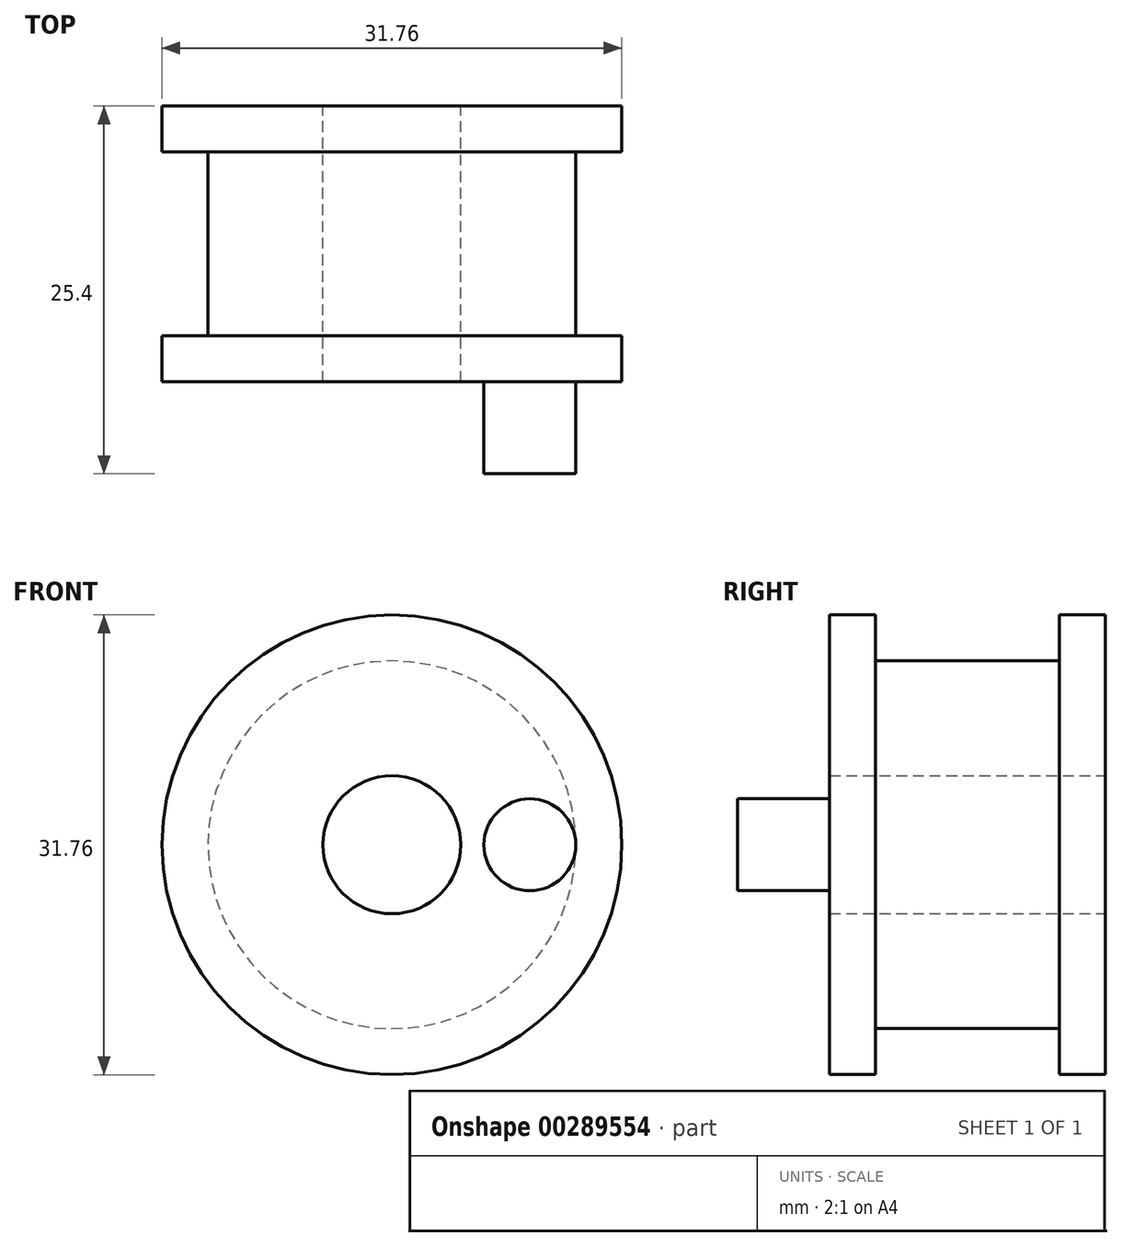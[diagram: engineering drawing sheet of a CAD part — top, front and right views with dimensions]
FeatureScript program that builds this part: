
annotation { "Feature Type Name" : "Feature", "Feature Type Description" : "" }
export const myFeature = defineFeature(function(context is Context, id is Id, definition is map)
    precondition{}
    {
        {
            var Q0;
            Q0=qCreatedBy(makeId("Front.planeOp"),FACE);
            var sketch = newSketch(context, id + "F0", { "sketchPlane" : qUnion([Q0])});
            skCircle(sketch, "E0", {"center": v(0, 0) * mm, "radius": 15.88 * mm});
            skCircle(sketch, "E1", {"center": v(0, 0) * mm, "radius": 4.76 * mm});
            skCircle(sketch, "E2", {"center": v(0, 0) * mm, "radius": 12.7 * mm});
            skSolve(sketch);
        }
        {
            var Q0;
            Q0=makeQuery(id+"F0.imprint","IMPRINT",FACE,{"disambiguationData":[TD([[makeQuery(id+"F0.imprint","IMPRINT",EDGE,{"derivedFrom":sQuery(id+"F0.wireOp",EDGE,"E0")}),1.0]])]});
            extrude(context, id + "F1", {"entities" : qUnion([Q0]), "depth" : 3.17 * mm});
        }
        {
            var Q0;
            Q0=makeQuery(id+"F0.imprint","IMPRINT",FACE,{"disambiguationData":[TD([[makeQuery(id+"F0.imprint","IMPRINT",EDGE,{"derivedFrom":sQuery(id+"F0.wireOp",EDGE,"E1")}),-1.0]])]});
            extrude(context, id + "F2", {"entities" : qUnion([Q0]), "operationType" : NewBodyOperationType.ADD, "depth" : 19.05 * mm});
        }
        {
            var Q0;
            Q0=makeQuery(id+"F2.opExtrude","CAP_FACE",FACE,{"disambiguationData":[OSD([sQuery(id+"F0.wireOp",EDGE,"E1"),sQuery(id+"F0.wireOp",EDGE,"E2")])],"isStart":false});
            var sketch = newSketch(context, id + "F3", { "sketchPlane" : qUnion([Q0])});
            skCircle(sketch, "E3", {"center": v(0, 0) * mm, "radius": 15.88 * mm});
            skCircle(sketch, "E4", {"center": v(0, 0) * mm, "radius": 4.76 * mm});
            skCircle(sketch, "E5", {"center": v(9.53, 0) * mm, "radius": 3.18 * mm});
            skSolve(sketch);
        }
        {
            var Q0;
            Q0 = qSketchRegion(id + "F3", true);
            extrude(context, id + "F4", {"entities" : qUnion([Q0]), "operationType" : NewBodyOperationType.ADD, "oppositeDirection" : true, "depth" : 3.17 * mm});
        }
        {
            var Q0;
            Q0=makeQuery(id+"F3.imprint","IMPRINT",FACE,{"disambiguationData":[TD([[makeQuery(id+"F3.imprint","IMPRINT",EDGE,{"derivedFrom":sQuery(id+"F3.wireOp",EDGE,"E5")}),1.0]])]});
            extrude(context, id + "F5", {"entities" : qUnion([Q0]), "operationType" : NewBodyOperationType.ADD, "depth" : 6.35 * mm});
        }
    });
